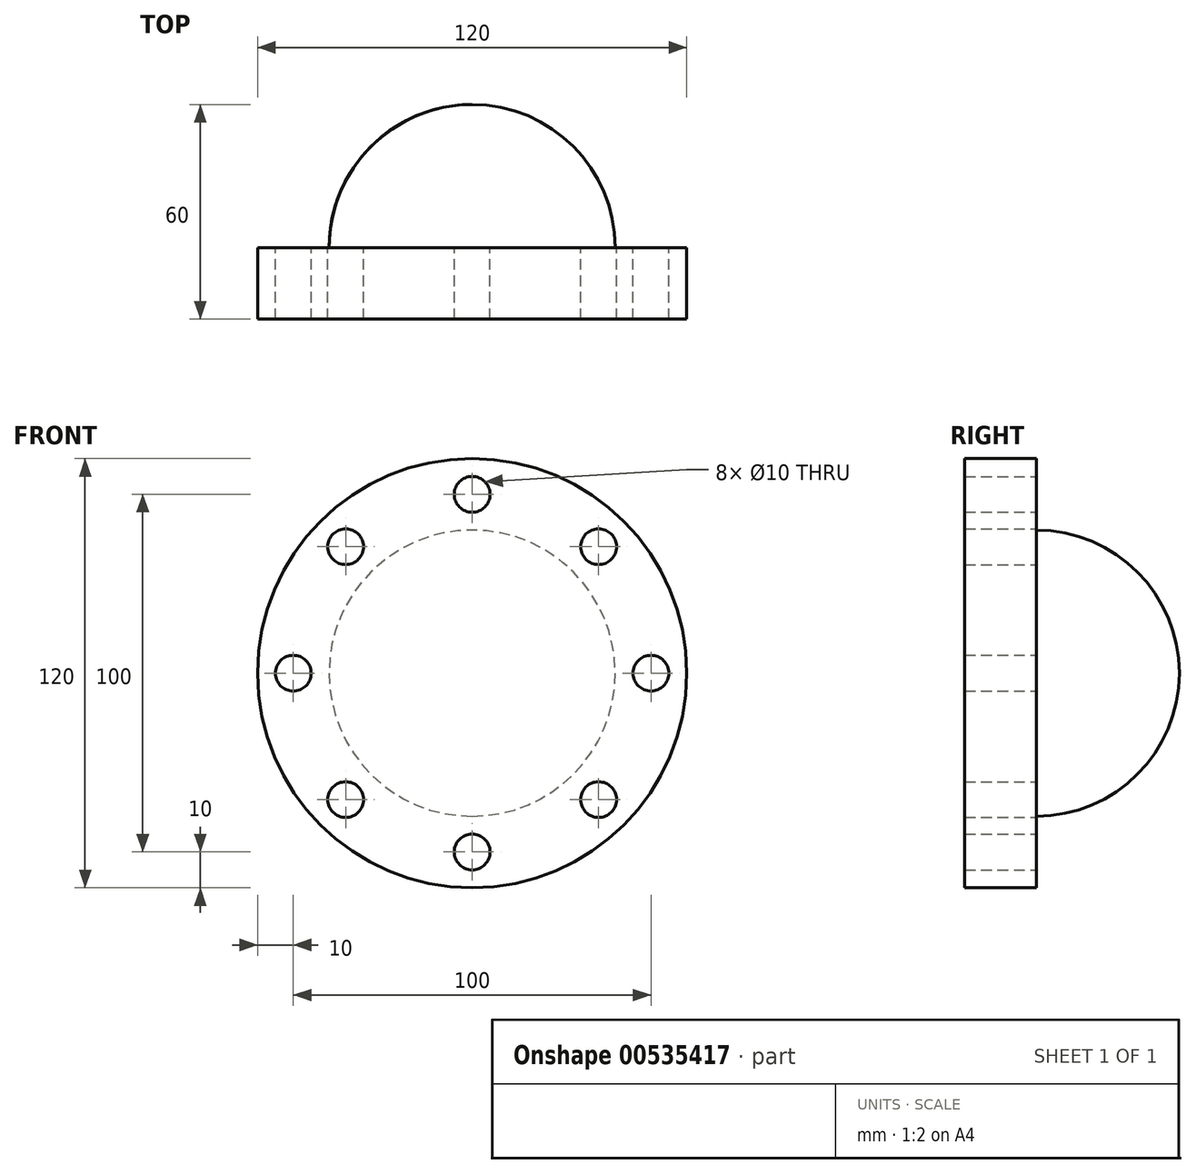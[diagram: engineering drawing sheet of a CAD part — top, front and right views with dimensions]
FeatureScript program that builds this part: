
annotation { "Feature Type Name" : "Feature", "Feature Type Description" : "" }
export const myFeature = defineFeature(function(context is Context, id is Id, definition is map)
    precondition{}
    {
        {
            var Q0;
            Q0=qCreatedBy(makeId("Front.planeOp"),FACE);
            var sketch = newSketch(context, id + "F0", { "sketchPlane" : qUnion([Q0])});
            skCircle(sketch, "E0", {"center": v(0, 0) * mm, "radius": 60 * mm});
            skCircle(sketch, "E1", {"center": v(0, 50) * mm, "radius": 5 * mm});
            skCircle(sketch, "E2.1.0", {"center": v(-35.36, 35.36) * mm, "radius": 5 * mm});
            skCircle(sketch, "E2.2.0", {"center": v(-50, 0) * mm, "radius": 5 * mm});
            skCircle(sketch, "E2.3.0", {"center": v(-35.36, -35.36) * mm, "radius": 5 * mm});
            skCircle(sketch, "E2.4.0", {"center": v(0, -50) * mm, "radius": 5 * mm});
            skCircle(sketch, "E2.5.0", {"center": v(35.36, -35.36) * mm, "radius": 5 * mm});
            skCircle(sketch, "E2.6.0", {"center": v(50, 0) * mm, "radius": 5 * mm});
            skCircle(sketch, "E2.7.0", {"center": v(35.36, 35.36) * mm, "radius": 5 * mm});
            skSolve(sketch);
        }
        {
            var Q0;
            Q0 = qSketchRegion(id + "F0", true);
            extrude(context, id + "F1", {"entities" : qUnion([Q0]), "depth" : 20 * mm, "offsetDistance" : 25 * mm});
        }
        {
            var Q0;
            Q0=qCreatedBy(makeId("Top.planeOp"),FACE);
            var sketch = newSketch(context, id + "F2", { "sketchPlane" : qUnion([Q0])});
            skLineSegment(sketch, "E3", {"start": v(60, 0) * mm, "end": v(60, -20) * mm});
            skLineSegment(sketch, "E4.0", {"start": v(60, 0) * mm, "end": v(-60, 0) * mm});
            skArc(sketch, "E5", {"start": v(0, 40) * mm, "mid": v(-28.28, 28.28) * mm, "end": v(-40, 0) * mm});
            skLineSegment(sketch, "E6", {"start": v(0, 0) * mm, "end": v(0, 40) * mm});
            skSolve(sketch);
        }
        {
            var Q0;
            {var subQ0=sQuery(id+"F2.wireOp",EDGE,"E5");Q0=makeQuery(id+"F2.imprint","IMPRINT",FACE,{"disambiguationData":[TD([[makeQuery(id+"F2.imprint","IMPRINT",EDGE,{"derivedFrom":subQ0}),1.0]])]});}
            var Q1;
            Q1=sQuery(id+"F2.wireOp",EDGE,"E6");
            revolve(context, id + "F3", {"operationType" : NewBodyOperationType.ADD, "entities" : qUnion([Q0]), "axis" : qUnion([Q1]), "revolveType" : RevolveType.FULL});
        }
    });
